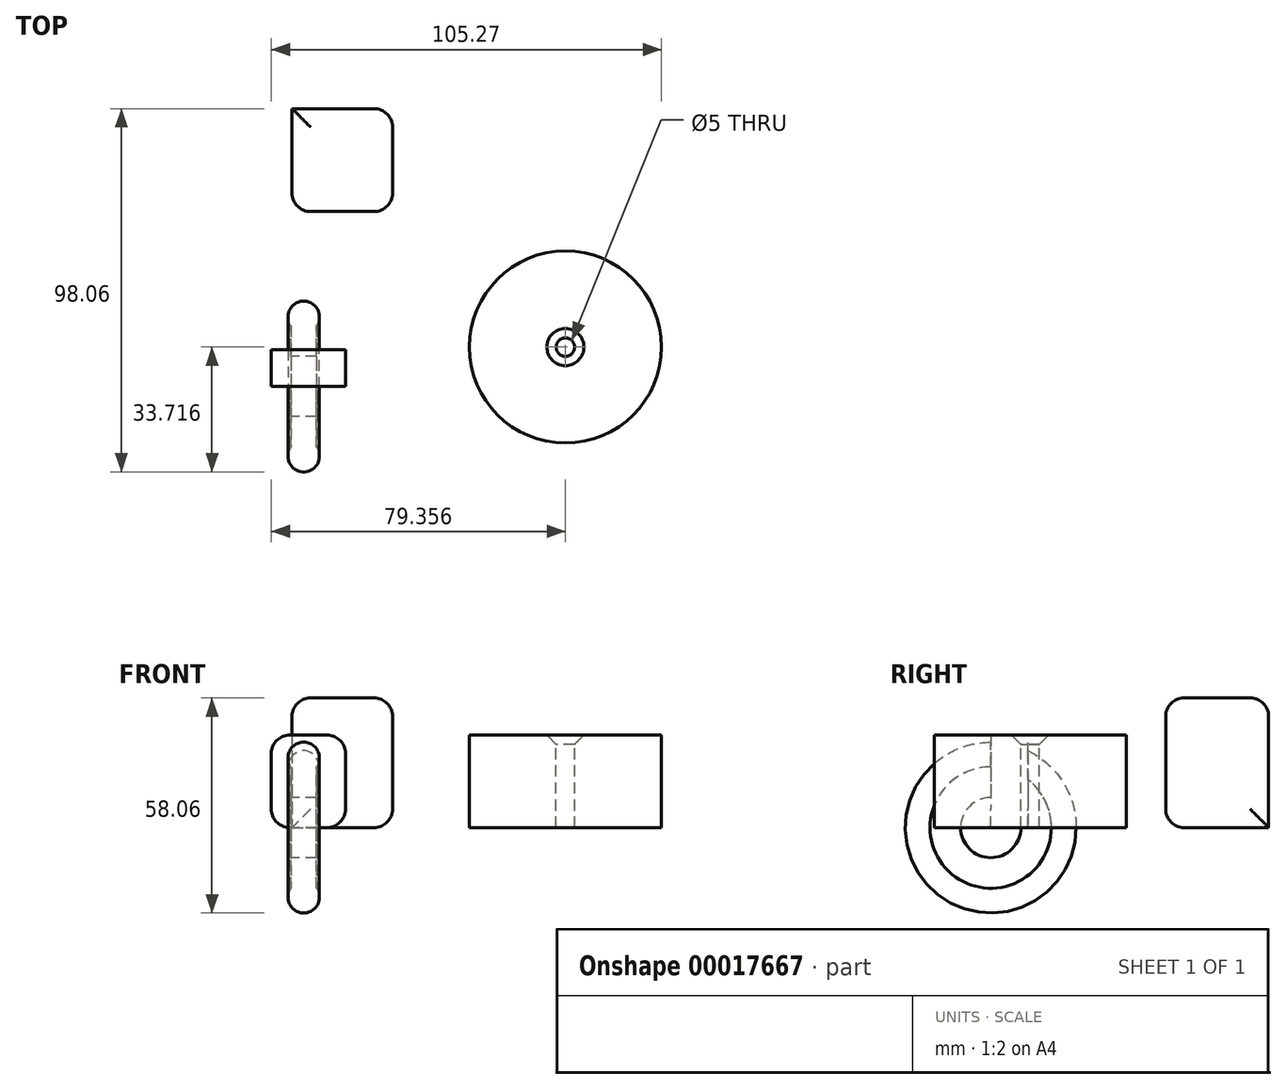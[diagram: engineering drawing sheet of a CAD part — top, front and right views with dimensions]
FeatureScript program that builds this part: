
annotation { "Feature Type Name" : "Feature", "Feature Type Description" : "" }
export const myFeature = defineFeature(function(context is Context, id is Id, definition is map)
    precondition{}
    {
        {
            var Q0;
            Q0=qCreatedBy(makeId("Top.planeOp"),FACE);
            var sketch = newSketch(context, id + "F0", { "sketchPlane" : qUnion([Q0])});
            skLineSegment(sketch, "E0.bottom", {"start": v(-60.43, -17.79) * mm, "end": v(-40.43, -17.79) * mm});
            skLineSegment(sketch, "E0.top", {"start": v(-60.43, -27.79) * mm, "end": v(-40.43, -27.79) * mm});
            skLineSegment(sketch, "E0.left", {"start": v(-60.43, -17.79) * mm, "end": v(-60.43, -27.79) * mm});
            skLineSegment(sketch, "E0.right", {"start": v(-40.43, -17.79) * mm, "end": v(-40.43, -27.79) * mm});
            skSolve(sketch);
        }
        {
            var Q0;
            Q0 = qSketchRegion(id + "F0", true);
            extrude(context, id + "F1", {"entities" : qUnion([Q0]), "depth" : 25 * mm});
        }
        {
            var Q0;
            Q0=makeQuery(id+"F1.opExtrude","CAP_EDGE",EDGE,{"disambiguationData":[OSD([sQuery(id+"F0.wireOp",EDGE,"E0.right")])],"isStart":false});
            var Q1;
            Q1=makeQuery(id+"F1.opExtrude","CAP_EDGE",EDGE,{"disambiguationData":[OSD([sQuery(id+"F0.wireOp",EDGE,"E0.left")])],"isStart":false});
            var Q2;
            Q2=makeQuery(id+"F1.opExtrude","CAP_EDGE",EDGE,{"disambiguationData":[OSD([sQuery(id+"F0.wireOp",EDGE,"E0.right")])],"isStart":true});
            var Q3;
            Q3=makeQuery(id+"F1.opExtrude","CAP_EDGE",EDGE,{"disambiguationData":[OSD([sQuery(id+"F0.wireOp",EDGE,"E0.left")])],"isStart":true});
            fillet(context, id + "F2", {"entities" : qUnion([Q0, Q1, Q2, Q3]), "radius" : 5 * mm, "tangentPropagation" : true, "allowEdgeOverflow" : false});
        }
        {
            var Q0;
            Q0=makeQuery(id+"F1.opExtrude","SWEPT_FACE",FACE,{"disambiguationData":[OSD([sQuery(id+"F0.wireOp",EDGE,"E0.top")])]});
            var sketch = newSketch(context, id + "F3", { "sketchPlane" : qUnion([Q0])});
            skLineSegment(sketch, "E1.top", {"start": v(-55.16, 8.13) * mm, "end": v(-48.22, 8.13) * mm});
            skLineSegment(sketch, "E1.left", {"start": v(-55.16, 16.37) * mm, "end": v(-55.16, 8.13) * mm});
            skLineSegment(sketch, "E1.right", {"start": v(-48.22, 16.37) * mm, "end": v(-48.22, 8.13) * mm});
            skArc(sketch, "E2", {"start": v(-48.22, 16.37) * mm, "mid": v(-51.7, 23.06) * mm, "end": v(-55.16, 16.37) * mm});
            skSolve(sketch);
        }
        {
            var Q0;
            Q0=makeQuery(id+"F3.imprint","IMPRINT",FACE,{"disambiguationData":[TD([[makeQuery(id+"F3.imprint","IMPRINT",EDGE,{"derivedFrom":sQuery(id+"F3.wireOp",EDGE,"E1.top")}),1.0]])]});
            var Q1;
            Q1=makeQuery(id+"F1.opExtrude","CAP_EDGE",EDGE,{"disambiguationData":[OSD([sQuery(id+"F0.wireOp",EDGE,"E0.top")])],"isStart":true});
            revolve(context, id + "F4", {"operationType" : NewBodyOperationType.ADD, "entities" : qUnion([Q0]), "axis" : qUnion([Q1]), "revolveType" : RevolveType.FULL});
        }
        {
            var Q0;
            Q0=qCreatedBy(makeId("Top.planeOp"),FACE);
            var sketch = newSketch(context, id + "F5", { "sketchPlane" : qUnion([Q0])});
            skCircle(sketch, "E3", {"center": v(18.93, -17.13) * mm, "radius": 25.92 * mm});
            skSolve(sketch);
        }
        {
            var Q0;
            Q0=makeQuery(id+"F5.imprint","IMPRINT",FACE,{"disambiguationData":[TD([[makeQuery(id+"F5.imprint","IMPRINT",EDGE,{"derivedFrom":sQuery(id+"F5.wireOp",EDGE,"E3")}),1.0]])]});
            extrude(context, id + "F6", {"entities" : qUnion([Q0]), "depth" : 25 * mm});
        }
        {
            var Q0;
            Q0=makeQuery(id+"F6.opExtrude","CAP_FACE",FACE,{"disambiguationData":[OSD([sQuery(id+"F5.wireOp",EDGE,"E3")])],"isStart":false});
            var sketch = newSketch(context, id + "F7", { "sketchPlane" : qUnion([Q0])});
            skPoint(sketch, "E4", {"position": v(18.93, -17.13) * mm});
            skSolve(sketch);
        }
        {
            var Q0;
            Q0=sQuery(id+"F7.wireOp",VERTEX,"E4");
            var Q1;
            Q1=makeQuery(id+"F6.opExtrude","SWEPT_BODY",BODY,{"disambiguationData":[OSD([sQuery(id+"F5.wireOp",EDGE,"E3")])]});
            hole(context, id + "F8", {"style" : HoleStyle.C_SINK, "holeDiameter" : 5 * mm, "cSinkDiameter" : 10 * mm, "endStyle" : HoleEndStyle.THROUGH, "locations" : qUnion([Q0]), "scope" : qUnion([Q1]), "cSinkAngle" : 90 * degree});
        }
        {
            var Q0;
            Q0=qCreatedBy(makeId("Top.planeOp"),FACE);
            var sketch = newSketch(context, id + "F9", { "sketchPlane" : qUnion([Q0])});
            skLineSegment(sketch, "E5.bottom", {"start": v(-54.84, 47.21) * mm, "end": v(-27.73, 47.21) * mm});
            skLineSegment(sketch, "E5.top", {"start": v(-54.84, 19.43) * mm, "end": v(-27.73, 19.43) * mm});
            skLineSegment(sketch, "E5.left", {"start": v(-54.84, 47.21) * mm, "end": v(-54.84, 19.43) * mm});
            skLineSegment(sketch, "E5.right", {"start": v(-27.73, 47.21) * mm, "end": v(-27.73, 19.43) * mm});
            skSolve(sketch);
        }
        {
            var Q0;
            Q0=makeQuery(id+"F9.imprint","IMPRINT",FACE,{"disambiguationData":[TD([[makeQuery(id+"F9.imprint","IMPRINT",EDGE,{"derivedFrom":sQuery(id+"F9.wireOp",EDGE,"E5.bottom")}),-1.0]])]});
            extrude(context, id + "F10", {"entities" : qUnion([Q0]), "depth" : 35 * mm});
        }
        {
            var Q0;
            Q0=makeQuery(id+"F10.opExtrude","SWEPT_FACE",FACE,{"disambiguationData":[OSD([sQuery(id+"F9.wireOp",EDGE,"E5.top")])]});
            var Q1;
            Q1=makeQuery(id+"F10.opExtrude","CAP_FACE",FACE,{"disambiguationData":[OSD([sQuery(id+"F9.wireOp",EDGE,"E5.bottom"),sQuery(id+"F9.wireOp",EDGE,"E5.top"),sQuery(id+"F9.wireOp",EDGE,"E5.left"),sQuery(id+"F9.wireOp",EDGE,"E5.right")])],"isStart":false});
            var Q2;
            Q2=makeQuery(id+"F10.opExtrude","SWEPT_FACE",FACE,{"disambiguationData":[OSD([sQuery(id+"F9.wireOp",EDGE,"E5.right")])]});
            fillet(context, id + "F11", {"entities" : qUnion([Q0, Q1, Q2]), "radius" : 5 * mm, "tangentPropagation" : true, "allowEdgeOverflow" : false});
        }
    });
